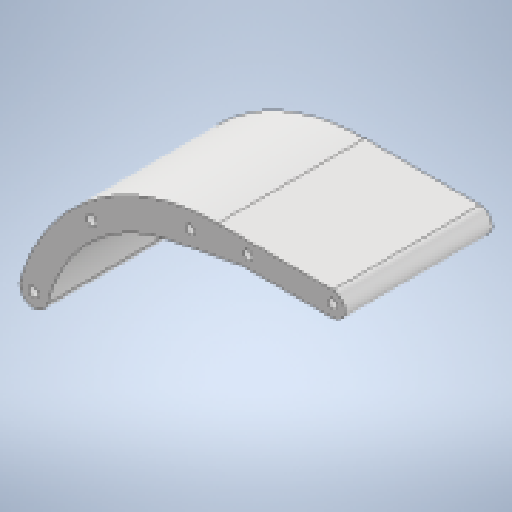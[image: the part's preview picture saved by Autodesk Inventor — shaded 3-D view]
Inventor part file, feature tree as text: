
AUTODESK INVENTOR PART (.ipt)
format: ipt  version: 2025.1 (Build 291241000, 241)  size: 164,864 bytes
history: native  units: mm
features: other x5, sketch x1, extrude x1, fillet x1, reference x1
ambient origin geometry x8: Origin, YZ Plane, XZ Plane, XY Plane, X Axis, Y Axis, Z Axis, Center Point
bodies: Body1 (feature_tree)
feature tree (9):
  other  "ソリッド1"
  sketch  "スケッチ1"
  other  "作業平面1"
  extrude  "押し出し1"  Depth=8.0mm
  fillet  "フィレット1"  Radius=1.6mm
  reference  "参照1"
  other  "<userpath>\Documents\Inventor\Vixen\doutai.iam"
  other  "doutai.iam"
  other  "tesaki:1"
